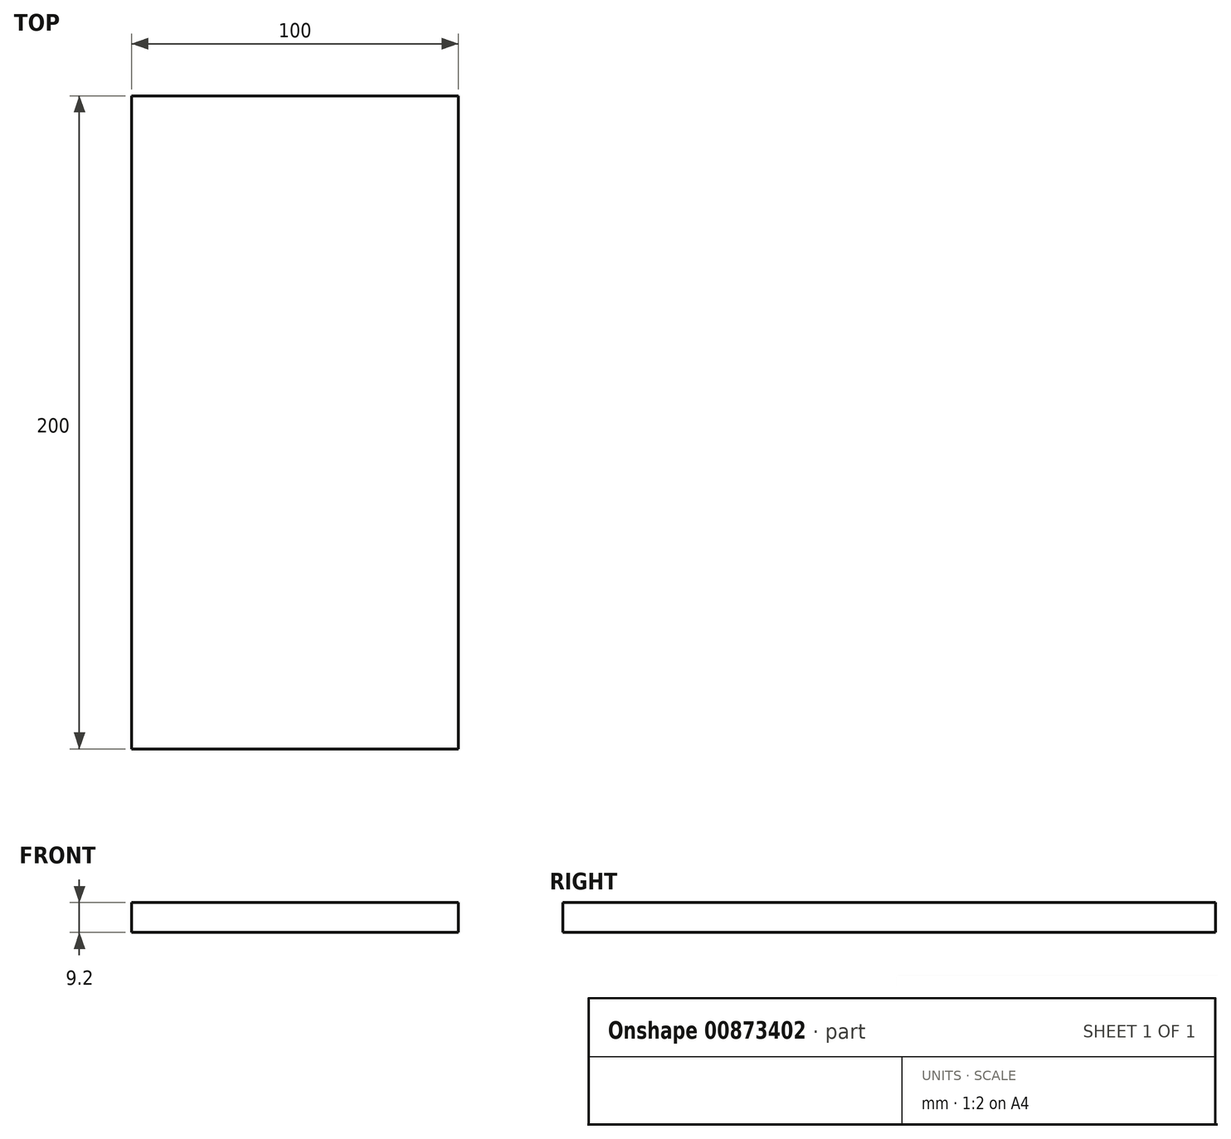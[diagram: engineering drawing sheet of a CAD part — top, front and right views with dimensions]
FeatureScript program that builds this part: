
annotation { "Feature Type Name" : "Feature", "Feature Type Description" : "" }
export const myFeature = defineFeature(function(context is Context, id is Id, definition is map)
    precondition{}
    {
        {
            var Q0;
            Q0=qCreatedBy(makeId("Top.planeOp"),FACE);
            var sketch = newSketch(context, id + "F0", { "sketchPlane" : qUnion([Q0])});
            skLineSegment(sketch, "E0.bottom", {"start": v(0, 0) * mm, "end": v(100, 0) * mm});
            skLineSegment(sketch, "E0.top", {"start": v(0, 200) * mm, "end": v(100, 200) * mm});
            skLineSegment(sketch, "E0.left", {"start": v(0, 0) * mm, "end": v(0, 200) * mm});
            skLineSegment(sketch, "E0.right", {"start": v(100, 0) * mm, "end": v(100, 200) * mm});
            skSolve(sketch);
        }
        {
            var Q0;
            Q0 = qSketchRegion(id + "F0", true);
            extrude(context, id + "F1", {"entities" : qUnion([Q0]), "depth" : 9.2 * mm, "offsetDistance" : 25 * mm});
        }
    });
